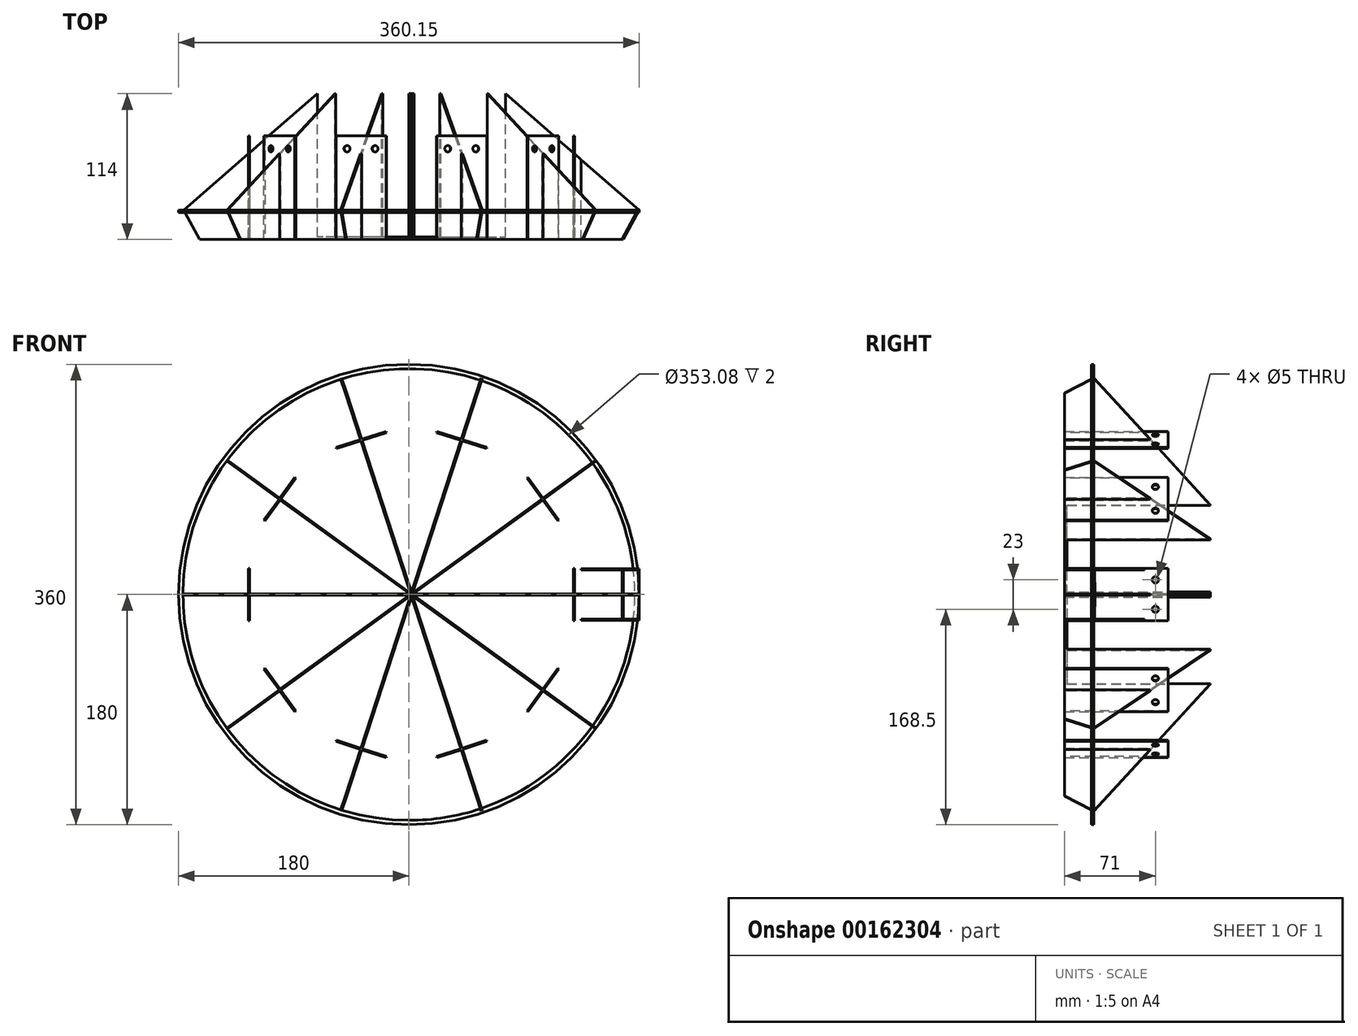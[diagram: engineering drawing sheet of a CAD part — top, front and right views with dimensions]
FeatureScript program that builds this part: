
annotation { "Feature Type Name" : "Feature", "Feature Type Description" : "" }
export const myFeature = defineFeature(function(context is Context, id is Id, definition is map)
    precondition{}
    {
        {
            var Q0;
            Q0=qCreatedBy(makeId("Top.planeOp"),FACE);
            var sketch = newSketch(context, id + "F0", { "sketchPlane" : qUnion([Q0])});
            skLineSegment(sketch, "E0", {"start": v(75.5, 0) * mm, "end": v(180, 0) * mm});
            skLineSegment(sketch, "E1", {"start": v(0, 0) * mm, "end": v(0, -23) * mm, "construction": true});
            skLineSegment(sketch, "E2", {"start": v(75.5, -23) * mm, "end": v(167.5, -23) * mm});
            skLineSegment(sketch, "E3", {"start": v(167.5, -23) * mm, "end": v(180, 0) * mm});
            skLineSegment(sketch, "E4", {"start": v(0, 91) * mm, "end": v(75.5, 91) * mm, "construction": true});
            skLineSegment(sketch, "E5", {"start": v(134.64, 39.5) * mm, "end": v(180, 0) * mm});
            skLineSegment(sketch, "E6", {"start": v(75.5, 39.5) * mm, "end": v(75.5, 0) * mm});
            skLineSegment(sketch, "E7", {"start": v(75.5, 0) * mm, "end": v(75.5, -23) * mm});
            skLineSegment(sketch, "E8", {"start": v(75.5, 0) * mm, "end": v(0, 0) * mm, "construction": true});
            skLineSegment(sketch, "E9", {"start": v(0, -23) * mm, "end": v(75.5, -23) * mm});
            skLineSegment(sketch, "E10", {"start": v(0, -23) * mm, "end": v(0, -21) * mm});
            skLineSegment(sketch, "E11", {"start": v(0, -21) * mm, "end": v(75.5, -21) * mm});
            skLineSegment(sketch, "E12", {"start": v(0, -21) * mm, "end": v(0, 91) * mm});
            skLineSegment(sketch, "E13", {"start": v(0, 91) * mm, "end": v(2, 91) * mm});
            skLineSegment(sketch, "E14", {"start": v(2, 91) * mm, "end": v(2, -21) * mm});
            skLineSegment(sketch, "E15", {"start": v(167.5, -23) * mm, "end": v(230.94, -23) * mm, "construction": true});
            skLineSegment(sketch, "E16", {"start": v(230.94, -23) * mm, "end": v(230.94, 39.5) * mm, "construction": true});
            skLineSegment(sketch, "E17", {"start": v(230.94, 39.5) * mm, "end": v(19.42, 39.5) * mm, "construction": true});
            skLineSegment(sketch, "E18", {"start": v(134.64, 39.5) * mm, "end": v(75.5, 39.5) * mm});
            skLineSegment(sketch, "E19", {"start": v(75.5, 39.5) * mm, "end": v(75.5, 91) * mm});
            skLineSegment(sketch, "E20", {"start": v(75.5, 91) * mm, "end": v(134.64, 39.5) * mm});
            skSolve(sketch);
        }
        {
            var Q0;
            Q0=qSketchRegion(id+"F0",true);
            extrude(context, id + "F1", {"entities" : qUnion([Q0]), "endBound" : BoundingType.SYMMETRIC, "depth" : 1 * mm});
        }
        {
            var Q0;
            Q0=qCreatedBy(makeId("Top.planeOp"),FACE);
            var sketch = newSketch(context, id + "F2", { "sketchPlane" : qUnion([Q0])});
            skLineSegment(sketch, "E21.bottom", {"start": v(15, 5.01) * mm, "end": v(21.3, 5.01) * mm});
            skLineSegment(sketch, "E21.top", {"start": v(15, 0) * mm, "end": v(21.3, 0) * mm});
            skLineSegment(sketch, "E21.left", {"start": v(15, 5.01) * mm, "end": v(15, 0) * mm});
            skLineSegment(sketch, "E21.right", {"start": v(21.3, 5.01) * mm, "end": v(21.3, 0) * mm});
            skSolve(sketch);
        }
        {
            var Q0;
            Q0=qSketchRegion(id+"F2",true);
            extrude(context, id + "F3", {"entities" : qUnion([Q0]), "operationType" : NewBodyOperationType.ADD, "endBound" : BoundingType.SYMMETRIC, "depth" : 38.5 * mm});
        }
        {
            var Q0;
            Q0=makeQuery(id+"F3.opExtrude","CAP_FACE",FACE,{"disambiguationData":[OSD([sQuery(id+"F2.wireOp",EDGE,"E21.bottom"),sQuery(id+"F2.wireOp",EDGE,"E21.top"),sQuery(id+"F2.wireOp",EDGE,"E21.left"),sQuery(id+"F2.wireOp",EDGE,"E21.right")])],"isStart":false});
            var sketch = newSketch(context, id + "F4", { "sketchPlane" : qUnion([Q0])});
            skLineSegment(sketch, "E22", {"start": v(75.5, 39.5) * mm, "end": v(75.5, -23) * mm, "construction": true});
            skLineSegment(sketch, "E23", {"start": v(134.5, 39.5) * mm, "end": v(134.64, 39.5) * mm});
            skLineSegment(sketch, "E24", {"start": v(134.64, 39.5) * mm, "end": v(180, 0) * mm});
            skLineSegment(sketch, "E25", {"start": v(180, 0) * mm, "end": v(167.5, -23) * mm});
            skLineSegment(sketch, "E26", {"start": v(167.5, -23) * mm, "end": v(134.5, -23) * mm});
            skLineSegment(sketch, "E27", {"start": v(134.5, -23) * mm, "end": v(134.5, 39.5) * mm});
            skLineSegment(sketch, "E28", {"start": v(75.5, -23) * mm, "end": v(134.5, -23) * mm, "construction": true});
            skLineSegment(sketch, "E29", {"start": v(75.5, 39.5) * mm, "end": v(134.64, 39.5) * mm, "construction": true});
            skSolve(sketch);
        }
        {
            var Q0;
            Q0=qSketchRegion(id+"F4",true);
            extrude(context, id + "F5", {"entities" : qUnion([Q0]), "depth" : 1 * mm});
        }
        {
            var Q0;
            Q0=makeQuery(id+"F5.opExtrude","SWEPT_FACE",FACE,{"disambiguationData":[OSD([sQuery(id+"F4.wireOp",EDGE,"E25")])]});
            var sketch = newSketch(context, id + "F6", { "sketchPlane" : qUnion([Q0])});
            skLineSegment(sketch, "E30", {"start": v(59.78, 19.25) * mm, "end": v(59.78, 0) * mm});
            skLineSegment(sketch, "E31", {"start": v(59.78, 0) * mm, "end": v(86.26, 0) * mm});
            skLineSegment(sketch, "E32", {"start": v(86.26, 0) * mm, "end": v(85.95, 20.25) * mm});
            skLineSegment(sketch, "E33", {"start": v(85.95, 20.25) * mm, "end": v(59.78, 20.25) * mm});
            skLineSegment(sketch, "E34", {"start": v(59.78, 20.25) * mm, "end": v(59.78, 19.25) * mm});
            skSolve(sketch);
        }
        {
            var Q0;
            Q0=qSketchRegion(id+"F6",true);
            extrude(context, id + "F7", {"entities" : qUnion([Q0]), "oppositeDirection" : true, "depth" : 1 * mm});
        }
        {
            var Q0;
            Q0=makeQuery(id+"F3.opExtrude","SWEPT_BODY",BODY,{"disambiguationData":[OSD([sQuery(id+"F2.wireOp",EDGE,"E21.bottom"),sQuery(id+"F2.wireOp",EDGE,"E21.top"),sQuery(id+"F2.wireOp",EDGE,"E21.left"),sQuery(id+"F2.wireOp",EDGE,"E21.right")])]});
            deleteBodies(context, id + "F8", {"entities" : qUnion([Q0])});
        }
        {
            var Q0;
            Q0=makeQuery(id+"F5.opExtrude","SWEPT_BODY",BODY,{"disambiguationData":[OSD([sQuery(id+"F4.wireOp",EDGE,"E22"),sQuery(id+"F4.wireOp",EDGE,"E23"),sQuery(id+"F4.wireOp",EDGE,"E24"),sQuery(id+"F4.wireOp",EDGE,"E25"),sQuery(id+"F4.wireOp",EDGE,"E26")])]});
            var Q1;
            Q1=makeQuery(id+"F7.opExtrude","SWEPT_BODY",BODY,{"disambiguationData":[OSD([sQuery(id+"F6.wireOp",EDGE,"E30"),sQuery(id+"F6.wireOp",EDGE,"E31"),sQuery(id+"F6.wireOp",EDGE,"E32"),sQuery(id+"F6.wireOp",EDGE,"E33"),sQuery(id+"F6.wireOp",EDGE,"E34")])]});
            var Q2;
            Q2=qCreatedBy(makeId("Top.planeOp"),FACE);
            mirror(context, id + "F9", {"entities" : qUnion([Q0, Q1]), "mirrorPlane" : qUnion([Q2])});
        }
        {
            var Q0;
            Q0=qCreatedBy(makeId("Top.planeOp"),FACE);
            var sketch = newSketch(context, id + "F10", { "sketchPlane" : qUnion([Q0])});
            skLineSegment(sketch, "E35", {"start": v(167.5, -23) * mm, "end": v(129.5, -23) * mm, "construction": true});
            skLineSegment(sketch, "E36", {"start": v(129.5, -23) * mm, "end": v(129.5, 58) * mm});
            skLineSegment(sketch, "E37", {"start": v(129.5, 58) * mm, "end": v(128.5, 58) * mm});
            skLineSegment(sketch, "E38", {"start": v(128.5, 58) * mm, "end": v(128.5, -23) * mm});
            skLineSegment(sketch, "E39", {"start": v(129.5, -23) * mm, "end": v(128.5, -23) * mm});
            skSolve(sketch);
        }
        {
            var Q0;
            Q0=qSketchRegion(id+"F10",true);
            extrude(context, id + "F11", {"entities" : qUnion([Q0]), "operationType" : NewBodyOperationType.ADD, "endBound" : BoundingType.SYMMETRIC, "depth" : 41 * mm});
        }
        {
            var Q0;
            Q0=makeQuery(id+"F11.opExtrude","SWEPT_FACE",FACE,{"disambiguationData":[OSD([sQuery(id+"F10.wireOp",EDGE,"E36")])]});
            var sketch = newSketch(context, id + "F12", { "sketchPlane" : qUnion([Q0])});
            skLineSegment(sketch, "E40", {"start": v(0, 0) * mm, "end": v(0, -11.5) * mm, "construction": true});
            skLineSegment(sketch, "E41", {"start": v(0, -11.5) * mm, "end": v(48, -11.5) * mm, "construction": true});
            skCircle(sketch, "E42", {"center": v(48, -11.5) * mm, "radius": 2.5 * mm});
            skLineSegment(sketch, "E43.MirrorCS", {"start": v(0, 11.5) * mm, "end": v(48, 11.5) * mm, "construction": true});
            skLineSegment(sketch, "E44.MirrorCS", {"start": v(0, 0) * mm, "end": v(0, 11.5) * mm, "construction": true});
            skCircle(sketch, "E45.MirrorC", {"center": v(48, 11.5) * mm, "radius": 2.5 * mm});
            skSolve(sketch);
        }
        {
            var Q0;
            Q0=qSketchRegion(id+"F12",true);
            extrude(context, id + "F13", {"entities" : qUnion([Q0]), "operationType" : NewBodyOperationType.REMOVE, "oppositeDirection" : true, "depth" : 25 * mm});
        }
        {
            var Q0;
            Q0=makeQuery(id+"F1.opExtrude","SWEPT_BODY",BODY,{"disambiguationData":[OSD([sQuery(id+"F0.wireOp",EDGE,"E2"),sQuery(id+"F0.wireOp",EDGE,"E3"),sQuery(id+"F0.wireOp",EDGE,"E5"),sQuery(id+"F0.wireOp",EDGE,"E6"),sQuery(id+"F0.wireOp",EDGE,"E7"),sQuery(id+"F0.wireOp",EDGE,"E9"),sQuery(id+"F0.wireOp",EDGE,"E10"),sQuery(id+"F0.wireOp",EDGE,"E11"),sQuery(id+"F0.wireOp",EDGE,"E12"),sQuery(id+"F0.wireOp",EDGE,"E13"),sQuery(id+"F0.wireOp",EDGE,"E14"),sQuery(id+"F0.wireOp",EDGE,"E19"),sQuery(id+"F0.wireOp",EDGE,"E20")])]});
            var Q1;
            Q1=sQuery(id+"F0.wireOp",EDGE,"E14");
            circularPattern(context, id + "F14", {"entities" : qUnion([Q0]), "axis" : qUnion([Q1]), "angle" : 36 * degree, "instanceCount" : 10});
        }
        {
            var Q0;
            Q0=qCreatedBy(makeId("Front.planeOp"),FACE);
            var sketch = newSketch(context, id + "F15", { "sketchPlane" : qUnion([Q0])});
            skCircle(sketch, "E46", {"center": v(0, 0) * mm, "radius": 180 * mm});
            skCircle(sketch, "E47", {"center": v(0, 0) * mm, "radius": 176.54 * mm});
            skSolve(sketch);
        }
        {
            var Q0;
            Q0=qSketchRegion(id+"F15",true);
            extrude(context, id + "F16", {"entities" : qUnion([Q0]), "depth" : 2 * mm});
        }
    });
